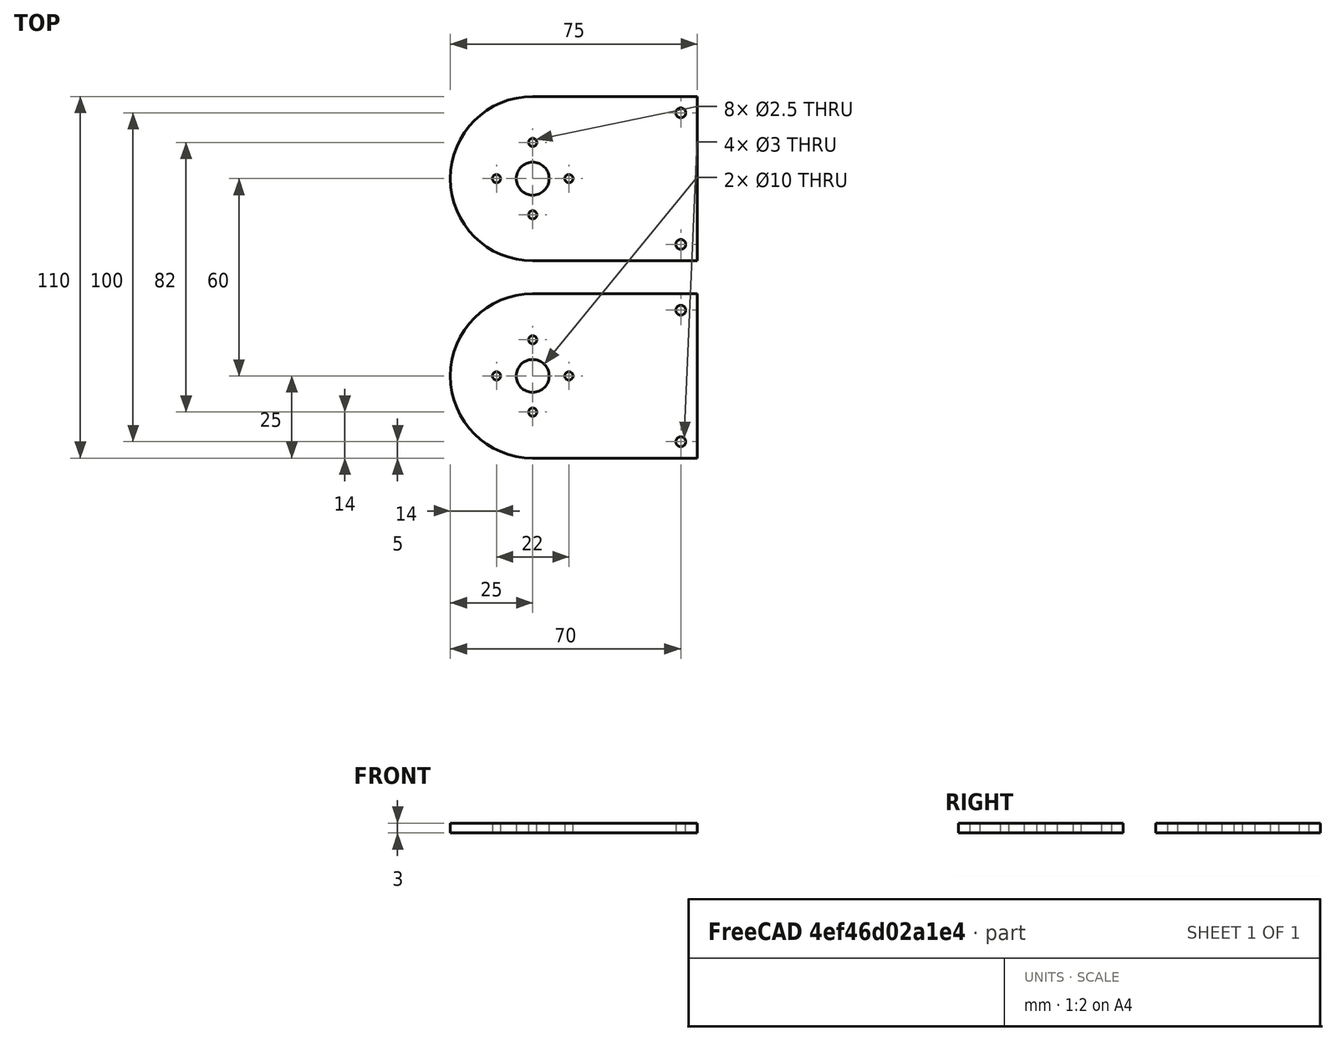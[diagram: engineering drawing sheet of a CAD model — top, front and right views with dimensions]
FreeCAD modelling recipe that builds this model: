
FCSTD DOCUMENT  (FreeCAD 1.0R39109 (Git))
Label: wrist
License: All rights reserved
LicenseURL: https://en.wikipedia.org/wiki/All_rights_reserved
objects: Sketcher::SketchObject×1, PartDesign::Pad×1, PartDesign::Body×1
note: 6 computed .brp shape members not serialized (recipe doc carries the construction recipe); baked Part::Feature solids carry a one-line shape summary decoded from their .brp

FEATURE [Sketcher::SketchObject] Sketch
  ArcFitTolerance = 1e-06
  AttachmentSupport = -> [XY_Plane]
  FullyConstrained = false
  MakeInternals = false
  MapMode = 5
  sketch-geometry (34):
    g0: ArcOfCircle CenterX=4.6e-15 CenterY=0 CenterZ=0 NormalX=0 NormalY=0 NormalZ=1 AngleXU=0 Radius=25 StartAngle=1.5708 EndAngle=4.71239
    g1: LineSegment [constr] StartX=4.6e-15 StartY=0 StartZ=0 EndX=4.6e-15 EndY=25 EndZ=0
    g2: LineSegment StartX=4.6e-15 StartY=25 StartZ=0 EndX=50 EndY=25 EndZ=0
    g3: LineSegment StartX=50 StartY=25 StartZ=0 EndX=50 EndY=-25 EndZ=0
    g4: LineSegment StartX=50 StartY=-25 StartZ=0 EndX=-3.19099e-07 EndY=-25 EndZ=0
    g5: Circle [constr] CenterX=4.6e-15 CenterY=0 CenterZ=0 NormalX=0 NormalY=0 NormalZ=1 AngleXU=0 Radius=11
    g6: LineSegment [constr] StartX=4.6e-15 StartY=0 StartZ=0 EndX=4.6e-15 EndY=11 EndZ=0
    g7: Circle CenterX=4.6e-15 CenterY=11 CenterZ=0 NormalX=0 NormalY=0 NormalZ=1 AngleXU=0 Radius=1.25
    g8: Circle CenterX=-11 CenterY=0 CenterZ=0 NormalX=0 NormalY=0 NormalZ=1 AngleXU=0 Radius=1.25
    g9: Circle CenterX=0 CenterY=-11 CenterZ=0 NormalX=0 NormalY=0 NormalZ=1 AngleXU=0 Radius=1.25
    g10: Circle CenterX=11 CenterY=0 CenterZ=0 NormalX=0 NormalY=0 NormalZ=1 AngleXU=0 Radius=1.25
    g11: LineSegment [constr] StartX=45 StartY=25 StartZ=0 EndX=45 EndY=-25 EndZ=0
    g12: LineSegment [constr] StartX=50 StartY=20 StartZ=0 EndX=45 EndY=20 EndZ=0
    g13: LineSegment [constr] StartX=50 StartY=-20 StartZ=0 EndX=45 EndY=-20 EndZ=0
    g14: Circle CenterX=45 CenterY=20 CenterZ=0 NormalX=0 NormalY=0 NormalZ=1 AngleXU=0 Radius=1.5
    g15: Circle CenterX=45 CenterY=-20 CenterZ=0 NormalX=0 NormalY=0 NormalZ=1 AngleXU=0 Radius=1.5
    g16: ArcOfCircle CenterX=3.1e-15 CenterY=-60 CenterZ=0 NormalX=0 NormalY=0 NormalZ=1 AngleXU=0 Radius=25 StartAngle=1.5708 EndAngle=4.71239
    g17: LineSegment [constr] StartX=3.1e-15 StartY=-60 StartZ=0 EndX=3.1e-15 EndY=-35 EndZ=0
    g18: LineSegment StartX=3.1e-15 StartY=-35 StartZ=0 EndX=50 EndY=-35 EndZ=0
    g19: LineSegment StartX=50 StartY=-35 StartZ=0 EndX=50 EndY=-85 EndZ=0
    g20: LineSegment StartX=50 StartY=-85 StartZ=0 EndX=6.85011e-05 EndY=-85 EndZ=0
    g21: Circle [constr] CenterX=3.1e-15 CenterY=-60 CenterZ=0 NormalX=0 NormalY=0 NormalZ=1 AngleXU=0 Radius=11
    g22: LineSegment [constr] StartX=3.1e-15 StartY=-60 StartZ=0 EndX=3.1e-15 EndY=-49 EndZ=0
    g23: Circle CenterX=3.1e-15 CenterY=-49 CenterZ=0 NormalX=0 NormalY=0 NormalZ=1 AngleXU=0 Radius=1.25
    g24: Circle CenterX=-11 CenterY=-60 CenterZ=0 NormalX=0 NormalY=0 NormalZ=1 AngleXU=0 Radius=1.25
    g25: Circle CenterX=0 CenterY=-71 CenterZ=0 NormalX=0 NormalY=0 NormalZ=1 AngleXU=0 Radius=1.25
    g26: Circle CenterX=11 CenterY=-60 CenterZ=0 NormalX=0 NormalY=0 NormalZ=1 AngleXU=0 Radius=1.25
    g27: LineSegment [constr] StartX=45 StartY=-35 StartZ=0 EndX=45 EndY=-85 EndZ=0
    g28: LineSegment [constr] StartX=50 StartY=-40 StartZ=0 EndX=45 EndY=-40 EndZ=0
    g29: LineSegment [constr] StartX=50 StartY=-80 StartZ=0 EndX=45 EndY=-80 EndZ=0
    g30: Circle CenterX=45 CenterY=-40 CenterZ=0 NormalX=0 NormalY=0 NormalZ=1 AngleXU=0 Radius=1.5
    g31: Circle CenterX=45 CenterY=-80 CenterZ=0 NormalX=0 NormalY=0 NormalZ=1 AngleXU=0 Radius=1.5
    g32: Circle CenterX=4.6e-15 CenterY=0 CenterZ=0 NormalX=0 NormalY=0 NormalZ=1 AngleXU=0 Radius=5
    g33: Circle CenterX=3.1e-15 CenterY=-60 CenterZ=0 NormalX=0 NormalY=0 NormalZ=1 AngleXU=0 Radius=5
  constraints (83):
    c: Coincident(g0,g-1)
    c: Diameter(g0) = 50
    c: Coincident(g1,g0)
    c: Vertical(g1)
    c: Coincident(g2,g1)
    c: Horizontal(g2)
    c: DistanceX(g2,g2) = 50
    c: Coincident(g3,g2)
    c: Vertical(g3)
    c: DistanceY(g3,g3) = 50
    c: Coincident(g4,g3)
    c: Horizontal(g4)
    c: Coincident(g0,g4)
    c: Coincident(g0,g1)
    c: Coincident(g5,g0)
    c: Diameter(g5) = 22
    c: Coincident(g6,g0)
    c: PointOnObject(g6,g5)
    c: Vertical(g6)
    c: Coincident(g7,g6)
    c: Diameter(g7) = 2.5
    c: Diameter(g8) = 2.5
    c: Diameter(g9) = 2.5
    c: Diameter(g10) = 2.5
    c: PointOnObject(g11,g2)
    c: PointOnObject(g11,g4)
    c: Vertical(g11)
    c: DistanceX(g11,g2) = 5
    c: PointOnObject(g12,g3)
    c: PointOnObject(g12,g11)
    c: Horizontal(g12)
    c: PointOnObject(g13,g3)
    c: PointOnObject(g13,g11)
    c: Horizontal(g13)
    c: DistanceY(g12,g2) = 5
    c: DistanceY(g3,g13) = 5
    c: Coincident(g14,g12)
    c: Coincident(g15,g13)
    c: Diameter(g14) = 3
    c: Equal(g15,g14)
    c: Diameter(g16) = 50
    c: Coincident(g17,g16)
    c: Vertical(g17)
    c: Coincident(g18,g17)
    c: Horizontal(g18)
    c: DistanceX(g18,g18) = 50
    c: Coincident(g19,g18)
    c: Vertical(g19)
    c: DistanceY(g19,g19) = 50
    c: Coincident(g20,g19)
    c: Horizontal(g20)
    c: Coincident(g16,g20)
    c: Coincident(g16,g17)
    c: Coincident(g21,g16)
    c: Diameter(g21) = 22
    c: Coincident(g22,g16)
    c: PointOnObject(g22,g21)
    c: Vertical(g22)
    c: Coincident(g23,g22)
    c: Diameter(g23) = 2.5
    c: Diameter(g24) = 2.5
    c: Diameter(g25) = 2.5
    c: Diameter(g26) = 2.5
    c: PointOnObject(g27,g18)
    c: PointOnObject(g27,g20)
    c: Vertical(g27)
    c: DistanceX(g27,g18) = 5
    c: PointOnObject(g28,g19)
    c: PointOnObject(g28,g27)
    c: Horizontal(g28)
    c: PointOnObject(g29,g19)
    c: PointOnObject(g29,g27)
    c: Horizontal(g29)
    c: DistanceY(g28,g18) = 5
    c: DistanceY(g19,g29) = 5
    c: Coincident(g30,g28)
    c: Coincident(g31,g29)
    c: Diameter(g30) = 3
    c: Equal(g31,g30)
    c: Coincident(g32,g0)
    c: Diameter(g32) = 10
    c: Coincident(g33,g16)
    c: Equal(g33,g32)
FEATURE [PartDesign::Pad] Pad
  Direction = (0,0,1)
  Length = 3
  Length2 = 10
  Profile = -> Sketch
  ReferenceAxis = -> Sketch [N_Axis]
  Refine = true
  Suppressed = false
  Type = 0
FEATURE [PartDesign::Body] Body
  AllowCompound = true
  Group = -> [Sketch,Pad]
  Origin = -> Origin
  Tip = -> Pad
